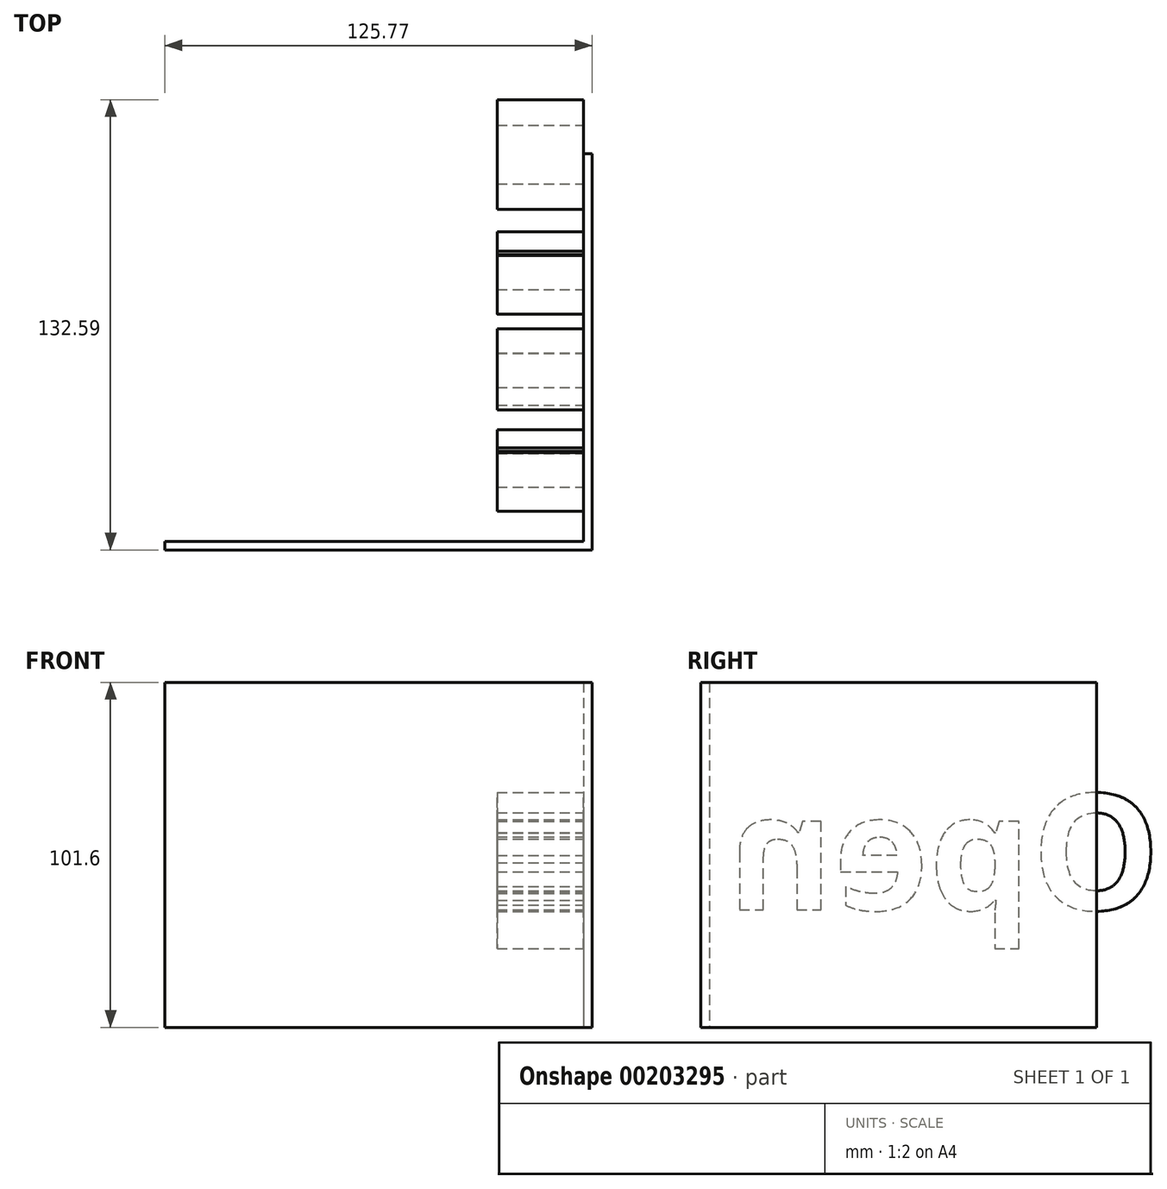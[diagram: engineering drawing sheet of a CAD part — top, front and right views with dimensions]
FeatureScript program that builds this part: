
annotation { "Feature Type Name" : "Feature", "Feature Type Description" : "" }
export const myFeature = defineFeature(function(context is Context, id is Id, definition is map)
    precondition{}
    {
        {
            var Q0;
            Q0=qCreatedBy(makeId("Top.planeOp"),FACE);
            var sketch = newSketch(context, id + "F0", { "sketchPlane" : qUnion([Q0])});
            skLineSegment(sketch, "E0.bottom", {"start": v(-61.22, 61.22) * mm, "end": v(64.55, 61.22) * mm});
            skLineSegment(sketch, "E0.top", {"start": v(-61.22, -55.46) * mm, "end": v(64.55, -55.46) * mm});
            skLineSegment(sketch, "E0.left", {"start": v(-61.22, 61.22) * mm, "end": v(-61.22, -55.46) * mm});
            skLineSegment(sketch, "E0.right", {"start": v(64.55, 61.22) * mm, "end": v(64.55, -55.46) * mm});
            skArc(sketch, "E1", {"start": v(-61.22, 61.22) * mm, "mid": v(-43.29, 17.93) * mm, "end": v(0, 0) * mm});
            skArc(sketch, "E2", {"start": v(64.55, 61.22) * mm, "mid": v(20.07, 43.48) * mm, "end": v(0, 0) * mm});
            skSolve(sketch);
        }
        {
            var Q0;
            Q0=makeQuery(id+"F0.imprint","IMPRINT",FACE,{"disambiguationData":[TD([[makeQuery(id+"F0.imprint","IMPRINT",EDGE,{"derivedFrom":sQuery(id+"F0.wireOp",EDGE,"E0.top")}),1.0]])]});
            var Q1;
            Q1=makeQuery(id+"F0.imprint","IMPRINT",FACE,{"disambiguationData":[TD([[makeQuery(id+"F0.imprint","IMPRINT",EDGE,{"derivedFrom":sQuery(id+"F0.wireOp",EDGE,"E0.bottom")}),-1.0]])]});
            extrude(context, id + "F1", {"entities" : qUnion([Q0, Q1]), "depth" : 101.6 * mm});
        }
        {
            var Q0;
            Q0=makeQuery(id+"F1.opExtrude","CAP_FACE",FACE,{"disambiguationData":[OSD([sQuery(id+"F0.wireOp",EDGE,"E0.bottom"),sQuery(id+"F0.wireOp",EDGE,"E0.top"),sQuery(id+"F0.wireOp",EDGE,"E0.left"),sQuery(id+"F0.wireOp",EDGE,"E0.right")])],"isStart":true});
            var Q1;
            Q1=makeQuery(id+"F1.opExtrude","SWEPT_FACE",FACE,{"disambiguationData":[OSD([sQuery(id+"F0.wireOp",EDGE,"E0.left")])]});
            var Q2;
            Q2=makeQuery(id+"F1.opExtrude","SWEPT_FACE",FACE,{"disambiguationData":[OSD([sQuery(id+"F0.wireOp",EDGE,"E0.bottom")])]});
            var Q3;
            Q3=makeQuery(id+"F1.opExtrude","CAP_FACE",FACE,{"disambiguationData":[OSD([sQuery(id+"F0.wireOp",EDGE,"E0.bottom"),sQuery(id+"F0.wireOp",EDGE,"E0.top"),sQuery(id+"F0.wireOp",EDGE,"E0.left"),sQuery(id+"F0.wireOp",EDGE,"E0.right")])],"isStart":false});
            shell(context, id + "F2", {"entities" : qUnion([Q0, Q1, Q2, Q3]), "thickness" : 2.54 * mm});
        }
        {
            var Q0;
            Q0=makeQuery(id+"F2.opShell","OFFSET_FACE",FACE,{"disambiguationData":[OSD([sQuery(id+"F0.wireOp",EDGE,"E0.right")])]});
            var sketch = newSketch(context, id + "F3", { "sketchPlane" : qUnion([Q0])});
            skText(sketch, "E3", { "text": "Open", "fontName": "OpenSans-Bold.ttf"});
            const initialGuessF3  = {"E3": [-0.0799, 0.03462, 1, 0, 0.0343]};
            skSetInitialGuess(sketch, initialGuessF3);
            skSolve(sketch);
        }
        {
            var Q0;
            Q0 = qSketchRegion(id + "F3", true);
            extrude(context, id + "F4", {"entities" : qUnion([Q0]), "operationType" : NewBodyOperationType.ADD, "depth" : 25.4 * mm});
        }
    });
